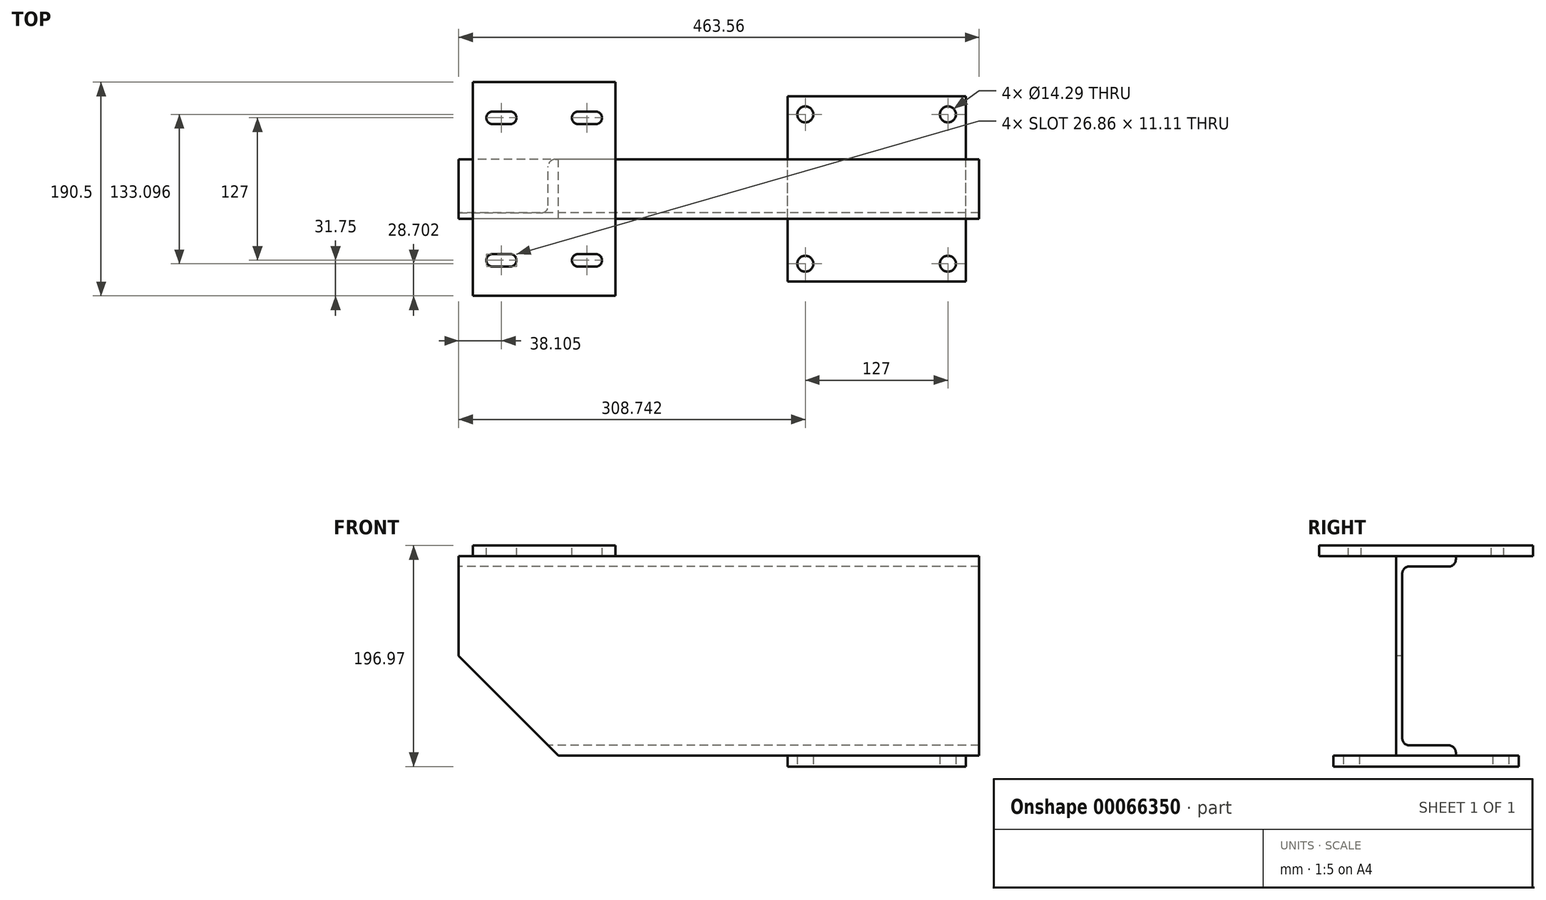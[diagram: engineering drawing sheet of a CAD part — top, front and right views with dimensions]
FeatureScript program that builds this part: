
annotation { "Feature Type Name" : "Feature", "Feature Type Description" : "" }
export const myFeature = defineFeature(function(context is Context, id is Id, definition is map)
    precondition{}
    {
        {
            var Q0;
            Q0=qCreatedBy(makeId("Right.planeOp"),FACE);
            var sketch = newSketch(context, id + "F0", { "sketchPlane" : qUnion([Q0])});
            skLineSegment(sketch, "E0", {"start": v(-57.59, 0) * mm, "end": v(57.95, 0) * mm});
            skLineSegment(sketch, "E1.0", {"start": v(-57.59, 177.8) * mm, "end": v(57.95, 177.8) * mm});
            skLineSegment(sketch, "E2", {"start": v(0, 0) * mm, "end": v(0, 9.14) * mm});
            skLineSegment(sketch, "E3.0", {"start": v(-26.54, 0) * mm, "end": v(-26.54, 177.8) * mm});
            skLineSegment(sketch, "E4.MirrorCS", {"start": v(26.54, 0) * mm, "end": v(26.54, 2.8) * mm});
            skLineSegment(sketch, "E5.0", {"start": v(-21.2, 15.5) * mm, "end": v(-21.2, 162.3) * mm});
            skLineSegment(sketch, "E6.0", {"start": v(-14.86, 9.14) * mm, "end": v(20.2, 9.14) * mm});
            skLineSegment(sketch, "E7.0", {"start": v(-14.86, 168.66) * mm, "end": v(20.2, 168.66) * mm});
            skLineSegment(sketch, "E8.trimOffspring", {"start": v(26.54, 175) * mm, "end": v(26.54, 177.8) * mm});
            skLineSegment(sketch, "E9.trimOffspring", {"start": v(0, 168.66) * mm, "end": v(0, 177.8) * mm});
            skArc(sketch, "E10.filletArc", {"start": v(-14.86, 168.66) * mm, "mid": v(-19.35, 166.8) * mm, "end": v(-21.2, 162.3) * mm});
            skArc(sketch, "E11.filletArc", {"start": v(-21.2, 15.5) * mm, "mid": v(-19.35, 11) * mm, "end": v(-14.86, 9.14) * mm});
            skArc(sketch, "E12.filletArc", {"start": v(26.54, 2.8) * mm, "mid": v(24.68, 7.28) * mm, "end": v(20.2, 9.14) * mm});
            skArc(sketch, "E13.filletArc", {"start": v(20.2, 168.66) * mm, "mid": v(24.68, 170.52) * mm, "end": v(26.54, 175) * mm});
            skSolve(sketch);
        }
        {
            var Q0;
            Q0=qSketchRegion(id+"F0",true);
            extrude(context, id + "F1", {"entities" : qUnion([Q0]), "endBound" : BoundingType.SYMMETRIC, "depth" : 463.55 * mm});
        }
        {
            var Q0;
            Q0=makeQuery(id+"F1.opExtrude","CAP_FACE",FACE,{"disambiguationData":[OSD([sQuery(id+"F0.wireOp",EDGE,"E0"),sQuery(id+"F0.wireOp",EDGE,"E1.0"),sQuery(id+"F0.wireOp",EDGE,"E3.0"),sQuery(id+"F0.wireOp",EDGE,"E4.MirrorCS"),sQuery(id+"F0.wireOp",EDGE,"E5.0"),sQuery(id+"F0.wireOp",EDGE,"E6.0"),sQuery(id+"F0.wireOp",EDGE,"E7.0"),sQuery(id+"F0.wireOp",EDGE,"E8.trimOffspring"),sQuery(id+"F0.wireOp",EDGE,"E10.filletArc"),sQuery(id+"F0.wireOp",EDGE,"E11.filletArc"),sQuery(id+"F0.wireOp",EDGE,"E12.filletArc"),sQuery(id+"F0.wireOp",EDGE,"E13.filletArc")])],"isStart":false});
            cPlane(context, id + "F2", {"entities" : qUnion([Q0]), "cplaneType" : CPlaneType.OFFSET, "offset" : 11.94 * mm, "oppositeDirection" : true, "width" : 152.4 * mm, "height" : 152.4 * mm});
        }
        {
            var Q0;
            Q0=qCreatedBy(id+"F2.planeOp",FACE);
            var sketch = newSketch(context, id + "F3", { "sketchPlane" : qUnion([Q0])});
            skLineSegment(sketch, "E14", {"start": v(0, 0) * mm, "end": v(0, -35.2) * mm, "construction": true});
            skLineSegment(sketch, "E15.0", {"start": v(-26.54, 0) * mm, "end": v(26.54, 0) * mm, "construction": true});
            skLineSegment(sketch, "E16.0", {"start": v(-82.55, 0) * mm, "end": v(-82.55, -35.2) * mm, "construction": true});
            skLineSegment(sketch, "E17.bottom", {"start": v(-82.55, 0) * mm, "end": v(82.55, 0) * mm});
            skLineSegment(sketch, "E17.top", {"start": v(-82.55, -9.65) * mm, "end": v(82.55, -9.65) * mm});
            skLineSegment(sketch, "E17.left", {"start": v(-82.55, 0) * mm, "end": v(-82.55, -9.65) * mm});
            skLineSegment(sketch, "E17.right", {"start": v(82.55, 0) * mm, "end": v(82.55, -9.65) * mm});
            skSolve(sketch);
        }
        {
            var Q0;
            Q0=qSketchRegion(id+"F3",true);
            extrude(context, id + "F4", {"entities" : qUnion([Q0]), "operationType" : NewBodyOperationType.ADD, "oppositeDirection" : true, "depth" : 158.75 * mm});
        }
        {
            var Q0;
            Q0=makeQuery(id+"F4.opExtrude","SWEPT_FACE",FACE,{"disambiguationData":[OSD([sQuery(id+"F3.wireOp",EDGE,"E17.top")])]});
            var sketch = newSketch(context, id + "F5", { "sketchPlane" : qUnion([Q0])});
            skLineSegment(sketch, "E18", {"start": v(140.46, 82.55) * mm, "end": v(140.46, -82.55) * mm, "construction": true});
            skLineSegment(sketch, "E19", {"start": v(219.84, 0) * mm, "end": v(61.09, 0) * mm, "construction": true});
            skLineSegment(sketch, "E20.0", {"start": v(76.96, 82.55) * mm, "end": v(76.96, -82.55) * mm, "construction": true});
            skLineSegment(sketch, "E21.0", {"start": v(219.84, 66.55) * mm, "end": v(61.09, 66.55) * mm, "construction": true});
            skPoint(sketch, "E22", {"position": v(76.96, 66.55) * mm});
            skPoint(sketch, "E23.MirrorP", {"position": v(76.96, -66.55) * mm});
            skPoint(sketch, "E24.MirrorP", {"position": v(203.96, -66.55) * mm});
            skPoint(sketch, "E25.MirrorP", {"position": v(203.96, 66.55) * mm});
            skSolve(sketch);
        }
        {
            var Q0;
            Q0=sQuery(id+"F5.wireOp",VERTEX,"E24.MirrorP");
            var Q1;
            Q1=sQuery(id+"F5.wireOp",VERTEX,"E23.MirrorP");
            var Q2;
            Q2=sQuery(id+"F5.wireOp",VERTEX,"E25.MirrorP");
            var Q3;
            Q3=sQuery(id+"F5.wireOp",VERTEX,"E22");
            var Q4;
            Q4=makeQuery(id+"F1.opExtrude","SWEPT_BODY",BODY,{"disambiguationData":[OSD([sQuery(id+"F0.wireOp",EDGE,"E0"),sQuery(id+"F0.wireOp",EDGE,"E1.0"),sQuery(id+"F0.wireOp",EDGE,"E3.0"),sQuery(id+"F0.wireOp",EDGE,"E4.MirrorCS"),sQuery(id+"F0.wireOp",EDGE,"E5.0"),sQuery(id+"F0.wireOp",EDGE,"E6.0"),sQuery(id+"F0.wireOp",EDGE,"E7.0"),sQuery(id+"F0.wireOp",EDGE,"E8.trimOffspring"),sQuery(id+"F0.wireOp",EDGE,"E10.filletArc"),sQuery(id+"F0.wireOp",EDGE,"E11.filletArc"),sQuery(id+"F0.wireOp",EDGE,"E12.filletArc"),sQuery(id+"F0.wireOp",EDGE,"E13.filletArc")])]});
            hole(context, id + "F6", {"style" : HoleStyle.SIMPLE, "holeDiameter" : 14.29 * mm, "endStyle" : HoleEndStyle.THROUGH, "locations" : qUnion([Q0, Q1, Q2, Q3]), "scope" : qUnion([Q4])});
        }
        {
            var Q0;
            Q0=makeQuery(id+"F1.opExtrude","CAP_FACE",FACE,{"disambiguationData":[OSD([sQuery(id+"F0.wireOp",EDGE,"E0"),sQuery(id+"F0.wireOp",EDGE,"E1.0"),sQuery(id+"F0.wireOp",EDGE,"E3.0"),sQuery(id+"F0.wireOp",EDGE,"E4.MirrorCS"),sQuery(id+"F0.wireOp",EDGE,"E5.0"),sQuery(id+"F0.wireOp",EDGE,"E6.0"),sQuery(id+"F0.wireOp",EDGE,"E7.0"),sQuery(id+"F0.wireOp",EDGE,"E8.trimOffspring"),sQuery(id+"F0.wireOp",EDGE,"E10.filletArc"),sQuery(id+"F0.wireOp",EDGE,"E11.filletArc"),sQuery(id+"F0.wireOp",EDGE,"E12.filletArc"),sQuery(id+"F0.wireOp",EDGE,"E13.filletArc")])],"isStart":true});
            cPlane(context, id + "F7", {"entities" : qUnion([Q0]), "cplaneType" : CPlaneType.OFFSET, "offset" : 76.2 * mm, "oppositeDirection" : true, "width" : 152.4 * mm, "height" : 152.4 * mm});
        }
        {
            var Q0;
            Q0=qCreatedBy(id+"F7.planeOp",FACE);
            var sketch = newSketch(context, id + "F8", { "sketchPlane" : qUnion([Q0])});
            skLineSegment(sketch, "E26.0", {"start": v(26.54, 177.8) * mm, "end": v(-95.25, 177.8) * mm});
            skLineSegment(sketch, "E27", {"start": v(0, 0) * mm, "end": v(0, 212.9) * mm, "construction": true});
            skLineSegment(sketch, "E28.0", {"start": v(-95.25, 0) * mm, "end": v(-95.25, 212.9) * mm, "construction": true});
            skPoint(sketch, "E29.orphan", {"position": v(-26.54, 177.8) * mm});
            skLineSegment(sketch, "E30.bottom", {"start": v(-95.25, 177.8) * mm, "end": v(95.25, 177.8) * mm});
            skLineSegment(sketch, "E30.top", {"start": v(-95.25, 187.32) * mm, "end": v(95.25, 187.32) * mm});
            skLineSegment(sketch, "E30.left", {"start": v(-95.25, 177.8) * mm, "end": v(-95.25, 187.32) * mm});
            skLineSegment(sketch, "E30.right", {"start": v(95.25, 177.8) * mm, "end": v(95.25, 187.32) * mm});
            skSolve(sketch);
        }
        {
            var Q0;
            Q0=qSketchRegion(id+"F8",true);
            extrude(context, id + "F9", {"entities" : qUnion([Q0]), "operationType" : NewBodyOperationType.ADD, "endBound" : BoundingType.SYMMETRIC, "depth" : 127 * mm});
        }
        {
            var Q0;
            Q0=makeQuery(id+"F9.opExtrude","SWEPT_FACE",FACE,{"disambiguationData":[OSD([sQuery(id+"F8.wireOp",EDGE,"E30.top")])]});
            var sketch = newSketch(context, id + "F10", { "sketchPlane" : qUnion([Q0])});
            skLineSegment(sketch, "E31", {"start": v(-155.58, 95.25) * mm, "end": v(-155.58, -95.25) * mm, "construction": true});
            skLineSegment(sketch, "E32", {"start": v(-219.08, 0) * mm, "end": v(-92.08, 0) * mm, "construction": true});
            skLineSegment(sketch, "E33.0", {"start": v(-193.68, 95.25) * mm, "end": v(-193.68, -95.25) * mm, "construction": true});
            skLineSegment(sketch, "E34", {"start": v(-185.8, -63.5) * mm, "end": v(-201.55, -63.5) * mm});
            skArc(sketch, "E35.0.startCap", {"start": v(-185.8, -57.94) * mm, "mid": v(-180.24, -63.5) * mm, "end": v(-185.8, -69.06) * mm});
            skArc(sketch, "E35.0.endCap", {"start": v(-201.55, -69.06) * mm, "mid": v(-207.1, -63.5) * mm, "end": v(-201.55, -57.94) * mm});
            skLineSegment(sketch, "E35.0.left", {"start": v(-185.8, -69.06) * mm, "end": v(-201.55, -69.06) * mm});
            skLineSegment(sketch, "E35.0.right", {"start": v(-185.8, -57.94) * mm, "end": v(-201.55, -57.94) * mm});
            skLineSegment(sketch, "E36.MirrorCS", {"start": v(-125.35, -57.94) * mm, "end": v(-109.6, -57.94) * mm});
            skLineSegment(sketch, "E37.MirrorCS", {"start": v(-125.35, -63.5) * mm, "end": v(-109.6, -63.5) * mm});
            skLineSegment(sketch, "E38.MirrorCS", {"start": v(-125.35, -69.06) * mm, "end": v(-109.6, -69.06) * mm});
            skArc(sketch, "E39.MirrorCS", {"start": v(-125.35, -57.94) * mm, "mid": v(-130.9, -63.5) * mm, "end": v(-125.35, -69.06) * mm});
            skArc(sketch, "E40.MirrorCS", {"start": v(-109.6, -69.06) * mm, "mid": v(-104.04, -63.5) * mm, "end": v(-109.6, -57.94) * mm});
            skArc(sketch, "E41.MirrorCS", {"start": v(-201.55, 69.06) * mm, "mid": v(-207.1, 63.5) * mm, "end": v(-201.55, 57.94) * mm});
            skLineSegment(sketch, "E42.MirrorCS", {"start": v(-185.8, 69.06) * mm, "end": v(-201.55, 69.06) * mm});
            skLineSegment(sketch, "E43.MirrorCS", {"start": v(-185.8, 63.5) * mm, "end": v(-201.55, 63.5) * mm});
            skArc(sketch, "E44.MirrorCS", {"start": v(-185.8, 57.94) * mm, "mid": v(-180.24, 63.5) * mm, "end": v(-185.8, 69.06) * mm});
            skLineSegment(sketch, "E45.MirrorCS", {"start": v(-185.8, 57.94) * mm, "end": v(-201.55, 57.94) * mm});
            skArc(sketch, "E46.MirrorCS", {"start": v(-125.35, 57.94) * mm, "mid": v(-130.9, 63.5) * mm, "end": v(-125.35, 69.06) * mm});
            skArc(sketch, "E47.MirrorCS", {"start": v(-109.6, 69.06) * mm, "mid": v(-104.04, 63.5) * mm, "end": v(-109.6, 57.94) * mm});
            skLineSegment(sketch, "E48.MirrorCS", {"start": v(-125.35, 63.5) * mm, "end": v(-109.6, 63.5) * mm});
            skLineSegment(sketch, "E49.MirrorCS", {"start": v(-125.35, 57.94) * mm, "end": v(-109.6, 57.94) * mm});
            skLineSegment(sketch, "E50.MirrorCS", {"start": v(-125.35, 69.06) * mm, "end": v(-109.6, 69.06) * mm});
            skSolve(sketch);
        }
        {
            var Q0;
            Q0=qSketchRegion(id+"F10",true);
            extrude(context, id + "F11", {"entities" : qUnion([Q0]), "operationType" : NewBodyOperationType.REMOVE, "endBound" : BoundingType.THROUGH_ALL, "oppositeDirection" : true, "depth" : 25.4 * mm});
        }
        {
            var Q0;
            Q0=makeQuery(id+"F1.opExtrude","CAP_EDGE",EDGE,{"disambiguationData":[OSD([sQuery(id+"F0.wireOp",EDGE,"E0")])],"isStart":true});
            chamfer(context, id + "F12", {"entities" : qUnion([Q0]), "width" : 88.9 * mm, "tangentPropagation" : true});
        }
    });
